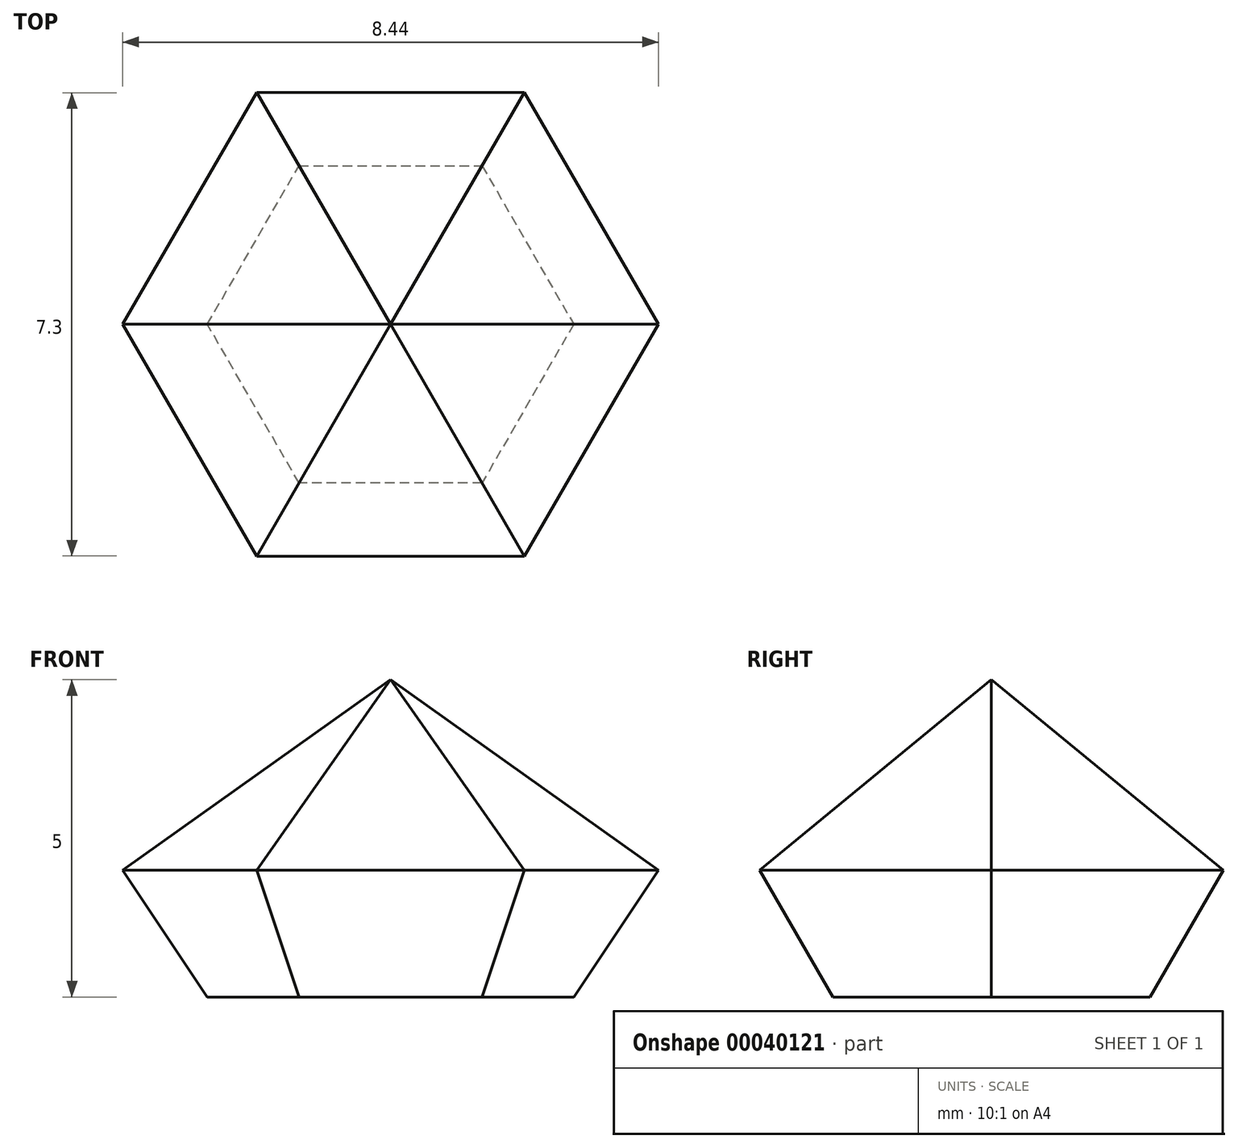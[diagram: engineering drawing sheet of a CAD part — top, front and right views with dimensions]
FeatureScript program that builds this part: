
annotation { "Feature Type Name" : "Feature", "Feature Type Description" : "" }
export const myFeature = defineFeature(function(context is Context, id is Id, definition is map)
    precondition{}
    {
        {
            var Q0;
            Q0=qCreatedBy(makeId("Top.planeOp"),FACE);
            var sketch = newSketch(context, id + "F0", { "sketchPlane" : qUnion([Q0])});
            skCircle(sketch, "E0.cCircle", {"center": v(0, 0) * mm, "radius": 2.5 * mm, "construction": true});
            skLineSegment(sketch, "E0.0", {"start": v(1.44, 2.5) * mm, "end": v(2.89, 0) * mm});
            skLineSegment(sketch, "E0.1", {"start": v(2.89, 0) * mm, "end": v(1.44, -2.5) * mm});
            skLineSegment(sketch, "E0.2", {"start": v(1.44, -2.5) * mm, "end": v(-1.44, -2.5) * mm});
            skLineSegment(sketch, "E0.3", {"start": v(-1.44, -2.5) * mm, "end": v(-2.89, 0) * mm});
            skLineSegment(sketch, "E0.4", {"start": v(-2.89, 0) * mm, "end": v(-1.44, 2.5) * mm});
            skLineSegment(sketch, "E0.5", {"start": v(-1.44, 2.5) * mm, "end": v(1.44, 2.5) * mm});
            skPoint(sketch, "E0.0.midPoint", {"position": v(2.17, 1.25) * mm});
            skSolve(sketch);
        }
        {
            var Q0;
            Q0 = qSketchRegion(id + "F0", true);
            extrude(context, id + "F1", {"entities" : qUnion([Q0]), "depth" : 2 * mm, "hasDraft" : true, "draftAngle" : 30 * degree});
        }
        {
            var Q0;
            Q0=qCreatedBy(makeId("Front.planeOp"),FACE);
            var sketch = newSketch(context, id + "F2", { "sketchPlane" : qUnion([Q0])});
            skLineSegment(sketch, "E1", {"start": v(0, 5) * mm, "end": v(0, 0) * mm});
            skSolve(sketch);
        }
        {
            var Q0;
            Q0=sQuery(id+"F2.wireOp",VERTEX,"E1.start");
            var Q1;
            Q1=makeQuery(id+"F1.opExtrude","CAP_VERTEX",VERTEX,{"disambiguationData":[OSD([sQuery(id+"F0.wireOp",EDGE,"E0.2"),sQuery(id+"F0.wireOp",EDGE,"E0.3")])],"isStart":false});
            var Q2;
            Q2=makeQuery(id+"F1.opExtrude","CAP_VERTEX",VERTEX,{"disambiguationData":[OSD([sQuery(id+"F0.wireOp",EDGE,"E0.1"),sQuery(id+"F0.wireOp",EDGE,"E0.2")])],"isStart":false});
            cPlane(context, id + "F3", {"entities" : qUnion([Q0, Q1, Q2]), "cplaneType" : CPlaneType.THREE_POINT, "offset" : 150 * mm, "width" : 150 * mm, "height" : 150 * mm});
        }
        {
            var Q0;
            Q0=qCreatedBy(id+"F3.planeOp",FACE);
            var sketch = newSketch(context, id + "F4", { "sketchPlane" : qUnion([Q0])});
            skLineSegment(sketch, "E2", {"start": v(0, -3.17) * mm, "end": v(-2.11, 1.56) * mm});
            skLineSegment(sketch, "E3", {"start": v(0, -3.17) * mm, "end": v(2.11, 1.56) * mm});
            skLineSegment(sketch, "E4.0", {"start": v(2.11, 1.56) * mm, "end": v(-2.11, 1.56) * mm});
            skSolve(sketch);
        }
        {
            var Q0;
            Q0 = qSketchRegion(id + "F4", true);
            extrude(context, id + "F5", {"entities" : qUnion([Q0]), "endBound" : BoundingType.UP_TO_NEXT, "depth" : 25 * mm});
        }
        {
            var Q0;
            Q0=makeQuery(id+"F5.opExtrude","SWEPT_BODY",BODY,{"disambiguationData":[OSD([sQuery(id+"F4.wireOp",EDGE,"E2"),sQuery(id+"F4.wireOp",EDGE,"E3"),sQuery(id+"F4.wireOp",EDGE,"E4.0")])]});
            var Q1;
            Q1=sQuery(id+"F2.wireOp",EDGE,"E1");
            circularPattern(context, id + "F6", {"operationType" : NewBodyOperationType.ADD, "entities" : qUnion([Q0]), "axis" : qUnion([Q1]), "angle" : 60 * degree, "instanceCount" : 6});
        }
    });
